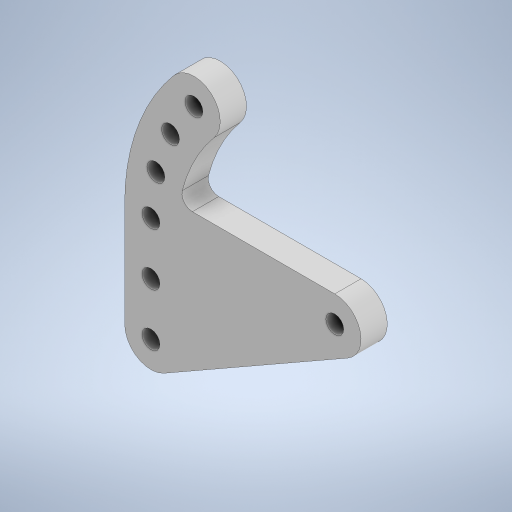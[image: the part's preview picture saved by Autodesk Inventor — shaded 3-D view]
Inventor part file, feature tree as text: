
AUTODESK INVENTOR PART (.ipt)
format: ipt  version: 2024.3 (Build 283343010, 343A)  size: 320,000 bytes
history: native  units: mm
features: sketch x7, extrude x5, projected_geometry x3, hole x2, other x1, fillet x1
ambient origin geometry x8: Origin, YZ Plane, XZ Plane, XY Plane, X Axis, Y Axis, Z Axis, Center Point
bodies: Body1 (feature_tree)
feature tree (19):
  other  "ソリッド1"
  extrude  "押し出し1"  Depth=80.0mm
  extrude  "押し出し2"  Depth=5.0mm TaperAngle=0.0deg
  hole  "穴1"  [1 undecoded]
  extrude  "押し出し3"  Depth=5.0mm
  extrude  "押し出し5"  Depth=10.0mm
  hole  "穴3"  [1 undecoded]
  extrude  "押し出し6"  Depth=70.0mm
  fillet  "フィレット1"  Radius=40.0mm
  sketch  "スケッチ1"
  sketch  "スケッチ2"
  projected_geometry  "投影ループ1"
  sketch  "スケッチ3"
  sketch  "スケッチ4"
  projected_geometry  "投影ループ2"
  sketch  "スケッチ7"
  sketch  "スケッチ8"
  sketch  "スケッチ9"
  projected_geometry  "投影ループ3"
note: 2 required parameter values undecoded (feature->parameter linkage not recoverable at this tier; creation-order binding heuristic only, values carry confidence <= 0.55)
